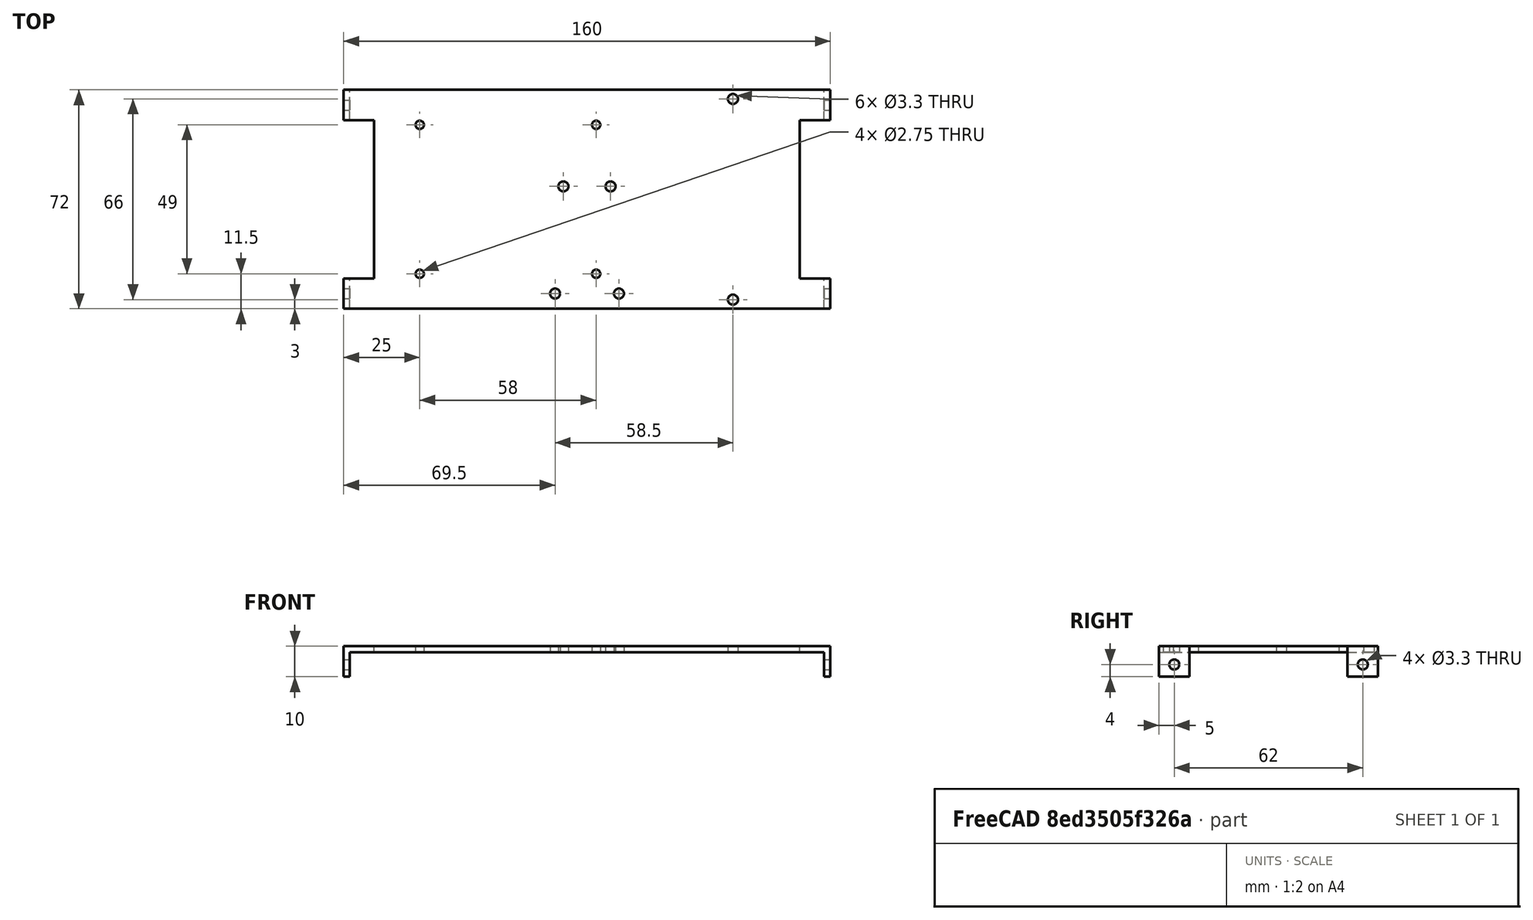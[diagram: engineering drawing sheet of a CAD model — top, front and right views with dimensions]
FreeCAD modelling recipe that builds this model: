
FCSTD DOCUMENT  (FreeCAD 0.17R13522 (Git))
Label: Zwischenblech_rpi
License: All rights reserved
LicenseURL: http://en.wikipedia.org/wiki/All_rights_reserved
objects: TechDraw::DrawViewDimension×25, Sketcher::SketchObject×4, PartDesign::Hole×4, Part::Box×3, Part::Cut×3, TechDraw::DrawProjGroupItem×3, Part::Mirroring×1, PartDesign::FeatureBase×1, TechDraw::DrawSVGTemplate×1, PartDesign::Body×1, TechDraw::DrawProjGroup×1, TechDraw::DrawPage×1
note: 21 computed .brp shape members not serialized (recipe doc carries the construction recipe); baked Part::Feature solids carry a one-line shape summary decoded from their .brp

FEATURE [Part::Box] Box  label="Würfel"
  AttacherType = Attacher::AttachEngine3D
  Height = 10
  Length = 160
  Width = 72
FEATURE [Part::Box] Box001  label="Würfel001"
  AttacherType = Attacher::AttachEngine3D
  Height = 10
  Length = 10
  Placement = pos=(0,10,0) rot=(0,0,1;0rad)
  Width = 52
FEATURE [Part::Mirroring] Part__Mirroring  label="Würfel001 (Mirror #1)"
  Base = (80,0,0)
  Normal = (1,0,0)
  Source = -> Box001
FEATURE [Part::Cut] Cut
  Base = -> Box
  Tool = -> Box001
FEATURE [Part::Cut] Cut001
  Base = -> Cut
  Tool = -> Part__Mirroring
FEATURE [Part::Box] Box002  label="Würfel002"
  AttacherType = Attacher::AttachEngine3D
  Height = 8
  Length = 156
  Placement = pos=(2,0,0) rot=(0,0,1;0rad)
  Width = 72
FEATURE [Part::Cut] Cut002
  Base = -> Cut001
  Tool = -> Box002
FEATURE [PartDesign::FeatureBase] BaseFeature
  BaseFeature = -> Cut002
FEATURE [Sketcher::SketchObject] Sketch
  MapMode = 5
  Placement = pos=(0,0,0) rot=(0.57735,-0.57735,-0.57735;2.0944rad)
  Support = -> [BaseFeature]
  sketch-geometry (2):
    g0: Circle CenterX=-5 CenterY=4 CenterZ=0 NormalX=0 NormalY=0 NormalZ=1 AngleXU=0 Radius=2.2
    g1: Circle CenterX=-67 CenterY=4 CenterZ=0 NormalX=0 NormalY=0 NormalZ=1 AngleXU=0 Radius=2.2
  constraints (6):
    c: Horizontal(g0,g1)
    c: DistanceY(g-1,g0) = 4
    c: Radius(g0) = 2.2
    c: Radius(g1) = 2.2
    c: DistanceX(g0,g-1) = 5
    c: DistanceX(g1,g-1) = 67
FEATURE [PartDesign::Hole] Hole
  BaseFeature = -> BaseFeature
  Depth = 25
  DepthType = 1
  Diameter = 3.3
  DrillPoint = 1
  DrillPointAngle = 118
  HoleCutCountersinkAngle = 90
  HoleCutDepth = 0
  HoleCutDiameter = 3
  HoleCutType = 0
  ModelActualThread = false
  Profile = -> Sketch
  Tapered = false
  TaperedAngle = 90
  ThreadAngle = 0
  ThreadClass = 0
  ThreadCutOffInner = 0
  ThreadCutOffOuter = 0
  ThreadDirection = 0
  ThreadFit = 0
  ThreadPitch = 0
  ThreadSize = 3
  ThreadType = 1
  Threaded = false
FEATURE [TechDraw::DrawSVGTemplate] Template
  EditableTexts = Designed_by_Name=Christian Dengler; FC-Date=25.04.2018; FC-SC=Scale; FC-SH=1/1; FC-Title=Zwischenblech, Oben
  Height = 210
  Orientation = 1
  Width = 297
FEATURE [Sketcher::SketchObject] Sketch001
  MapMode = 5
  Placement = pos=(0,0,10) rot=(0,0,1;0rad)
  Support = -> [Hole]
  sketch-geometry (4):
    g0: Circle CenterX=72.25 CenterY=40.25 CenterZ=0 NormalX=0 NormalY=0 NormalZ=1 AngleXU=0 Radius=1.65
    g1: Circle CenterX=87.75 CenterY=40.25 CenterZ=0 NormalX=0 NormalY=0 NormalZ=1 AngleXU=0 Radius=1.65
    g2: Circle CenterX=128 CenterY=69 CenterZ=0 NormalX=0 NormalY=0 NormalZ=1 AngleXU=0 Radius=2
    g3: Circle CenterX=128 CenterY=3 CenterZ=0 NormalX=0 NormalY=0 NormalZ=1 AngleXU=0 Radius=2
  constraints (12):
    c: Horizontal(g0,g1)
    c: Vertical(g2,g3)
    c: DistanceX(g-1,g0) = 72.25
    c: DistanceX(g0,g1) = 15.5
    c: DistanceY(g-1,g0) = 40.25
    c: Radius(g0) = 1.65
    c: Radius(g1) = 1.65
    c: DistanceY(g3,g2) = 66
    c: Radius(g2) = 2
    c: Radius(g3) = 2
    c: DistanceX(g-1,g3) = 128
    c: DistanceY(g-1,g3) = 3
FEATURE [Sketcher::SketchObject] Sketch002
  MapMode = 5
  Placement = pos=(0,0,10) rot=(0,0,1;0rad)
  Support = -> [Hole]
  sketch-geometry (4):
    g0: Circle CenterX=25 CenterY=60.5 CenterZ=0 NormalX=0 NormalY=0 NormalZ=1 AngleXU=0 Radius=1.375
    g1: Circle CenterX=83 CenterY=60.5 CenterZ=0 NormalX=0 NormalY=0 NormalZ=1 AngleXU=0 Radius=1.375
    g2: Circle CenterX=25 CenterY=11.5 CenterZ=0 NormalX=0 NormalY=0 NormalZ=1 AngleXU=0 Radius=1.375
    g3: Circle CenterX=83 CenterY=11.5 CenterZ=0 NormalX=0 NormalY=0 NormalZ=1 AngleXU=0 Radius=1.375
  constraints (12):
    c: Radius(g0) = 1.375
    c: Radius(g1) = 1.375
    c: Radius(g2) = 1.375
    c: Radius(g3) = 1.375
    c: Vertical(g2,g0)
    c: Vertical(g1,g3)
    c: Horizontal(g2,g3)
    c: Horizontal(g0,g1)
    c: DistanceY(g2,g0) = 49
    c: DistanceX(g2,g3) = 58
    c: DistanceX(g-1,g2) = 25
    c: DistanceY(g-1,g2) = 11.5
FEATURE [PartDesign::Hole] Hole001
  BaseFeature = -> Hole
  Depth = 25
  DepthType = 1
  Diameter = 3.3
  DrillPoint = 1
  DrillPointAngle = 118
  HoleCutCountersinkAngle = 90
  HoleCutDepth = 0
  HoleCutDiameter = 3
  HoleCutType = 0
  ModelActualThread = false
  Profile = -> Sketch001
  Tapered = false
  TaperedAngle = 90
  ThreadAngle = 0
  ThreadClass = 0
  ThreadCutOffInner = 0
  ThreadCutOffOuter = 0
  ThreadDirection = 0
  ThreadFit = 0
  ThreadPitch = 0
  ThreadSize = 3
  ThreadType = 1
  Threaded = false
FEATURE [PartDesign::Hole] Hole002
  BaseFeature = -> Hole001
  Depth = 25
  DepthType = 1
  Diameter = 2.75
  DrillPoint = 1
  DrillPointAngle = 118
  HoleCutCountersinkAngle = 90
  HoleCutDepth = 0
  HoleCutDiameter = 2.5
  HoleCutType = 0
  ModelActualThread = false
  Profile = -> Sketch002
  Tapered = false
  TaperedAngle = 90
  ThreadAngle = 0
  ThreadClass = 0
  ThreadCutOffInner = 0
  ThreadCutOffOuter = 0
  ThreadDirection = 0
  ThreadFit = 0
  ThreadPitch = 0
  ThreadSize = 2
  ThreadType = 1
  Threaded = false
FEATURE [Sketcher::SketchObject] Sketch003
  MapMode = 5
  Placement = pos=(0,0,10) rot=(0,0,1;0rad)
  Support = -> [Hole002]
  sketch-geometry (2):
    g0: Circle CenterX=69.5 CenterY=5 CenterZ=0 NormalX=0 NormalY=0 NormalZ=1 AngleXU=0 Radius=1.65
    g1: Circle CenterX=90.5 CenterY=5 CenterZ=0 NormalX=0 NormalY=0 NormalZ=1 AngleXU=0 Radius=1.65
  constraints (6):
    c: Horizontal(g0,g1)
    c: DistanceX(g0,g1) = 21
    c: Radius(g0) = 1.65
    c: Radius(g1) = 1.65
    c: DistanceX(g-1,g0) = 69.5
    c: DistanceY(g-1,g0) = 5
FEATURE [PartDesign::Hole] Hole003
  BaseFeature = -> Hole002
  Depth = 25
  DepthType = 0
  Diameter = 3.3
  DrillPoint = 1
  DrillPointAngle = 118
  HoleCutCountersinkAngle = 90
  HoleCutDepth = 0
  HoleCutDiameter = 3
  HoleCutType = 0
  ModelActualThread = false
  Profile = -> Sketch003
  Tapered = false
  TaperedAngle = 90
  ThreadAngle = 0
  ThreadClass = 0
  ThreadCutOffInner = 0
  ThreadCutOffOuter = 0
  ThreadDirection = 0
  ThreadFit = 0
  ThreadPitch = 0
  ThreadSize = 3
  ThreadType = 1
  Threaded = false
FEATURE [PartDesign::Body] Body
  BaseFeature = -> Cut002
  Group = -> [BaseFeature,Sketch,Hole,Sketch001,Sketch002,Hole001,Hole002,Sketch003,Hole003]
  Origin = -> Origin
  Tip = -> Hole003
FEATURE [TechDraw::DrawProjGroupItem] ProjItem001  label="Top"
  CoarseView = false
  Direction = (0,0,1)
  Focus = 100
  HardHidden = false
  IsoCount = 0
  IsoHidden = false
  IsoVisible = false
  LockPosition = false
  Perspective = false
  Rotation = 0
  RotationVector = (1,0,0)
  ScaleType = 0
  SeamHidden = false
  SeamVisible = false
  SmoothHidden = false
  SmoothVisible = false
  Source = -> [Body]
  Type = 4
  X = 0
  Y = -72.6
FEATURE [TechDraw::DrawProjGroupItem] ProjItem  label="Front"
  CoarseView = false
  Direction = (0,-1,0)
  Focus = 100
  HardHidden = false
  IsoCount = 0
  IsoHidden = false
  IsoVisible = false
  LockPosition = false
  Perspective = false
  Rotation = 0
  RotationVector = (1,0,0)
  ScaleType = 0
  SeamHidden = false
  SeamVisible = false
  SmoothHidden = false
  SmoothVisible = false
  Source = -> [Body]
  Type = 0
  X = 0
  Y = 63.9337
FEATURE [TechDraw::DrawProjGroupItem] ProjItem002  label="Left"
  CoarseView = false
  Direction = (-1,0,0)
  Focus = 100
  HardHidden = false
  IsoCount = 0
  IsoHidden = false
  IsoVisible = false
  LockPosition = true
  Perspective = false
  Rotation = 0
  RotationVector = (0,1,0)
  ScaleType = 0
  SeamHidden = false
  SeamVisible = false
  SmoothHidden = false
  SmoothVisible = false
  Source = -> [Body]
  Type = 1
  X = 132.721
  Y = 0
FEATURE [TechDraw::DrawProjGroup] ProjGroup
  Anchor = -> ProjItem
  AutoDistribute = true
  CubeDirs = (6) [(1.22465e-16,-2.44929e-16,-1),(1.93086e-32,-1,2.44929e-16),(-1,-2.46519e-32,-1.22465e-16),(-1.93086e-32,1,-2.44929e-16),(1,2.46519e-32,1.22465e-16),(-1.22465e-16,2.44929e-16,1)]
  CubeRotations = (6) [(1,2.46519e-32,1.22465e-16),(1,2.46519e-32,1.22465e-16),(4.89859e-16,1,-3.67394e-16),(-1,-2.46519e-32,-1.22465e-16),(-4.89859e-16,-1,3.67394e-16),(1,2.46519e-32,1.22465e-16)]
  LockPosition = false
  ProjectionType = 0
  Rotation = 0
  Scale = 0.8
  ScaleType = 2
  Source = -> [Body]
  Views = -> [ProjItem,ProjItem001,ProjItem002]
  X = 107.188
  Y = 189.377
  spacingX = 15
  spacingY = 15
FEATURE [TechDraw::DrawViewDimension] Dimension
  FormatSpec = %.2f
  LockPosition = false
  MeasureType = 1
  References2D = -> [ProjItem001]
  Rotation = 0
  ScaleType = 0
  Type = 1
  X = -5.19276
  Y = 38.5748
FEATURE [TechDraw::DrawViewDimension] Dimension001
  FormatSpec = %.2f
  LockPosition = false
  MeasureType = 1
  References2D = -> [ProjItem001]
  Rotation = 0
  ScaleType = 0
  Type = 1
  X = -6.12004
  Y = 46.7348
FEATURE [TechDraw::DrawViewDimension] Dimension002
  FormatSpec = %.2f
  LockPosition = false
  MeasureType = 1
  References2D = -> [ProjItem001]
  Rotation = 0
  ScaleType = 0
  Type = 1
  X = -6.86186
  Y = 55.8222
FEATURE [TechDraw::DrawViewDimension] Dimension003
  FormatSpec = %.2f
  LockPosition = false
  MeasureType = 1
  References2D = -> [ProjItem001]
  Rotation = 0
  ScaleType = 0
  Type = 2
  X = -90.1814
  Y = -6.72017
FEATURE [TechDraw::DrawViewDimension] Dimension004
  FormatSpec = %.2f
  LockPosition = false
  MeasureType = 1
  References2D = -> [ProjItem001]
  Rotation = 0
  ScaleType = 0
  Type = 1
  X = -25.9025
  Y = -54.5137
FEATURE [TechDraw::DrawViewDimension] Dimension006
  FormatSpec = %.2f
  LockPosition = false
  MeasureType = 1
  References2D = -> [ProjItem001]
  Rotation = 0
  ScaleType = 0
  Type = 1
  X = -24.0799
  Y = -97.174
FEATURE [TechDraw::DrawViewDimension] Dimension007
  FormatSpec = %.2f
  LockPosition = false
  MeasureType = 1
  References2D = -> [ProjItem001]
  Rotation = 0
  ScaleType = 0
  Type = 1
  X = -24.0703
  Y = -78.1047
FEATURE [TechDraw::DrawViewDimension] Dimension008
  FormatSpec = %.2f
  LockPosition = false
  MeasureType = 1
  References2D = -> [ProjItem001]
  Rotation = 0
  ScaleType = 0
  Type = 1
  X = -25.9902
  Y = -69.6317
FEATURE [TechDraw::DrawViewDimension] Dimension009
  FormatSpec = %.2f
  LockPosition = false
  MeasureType = 1
  References2D = -> [ProjItem001]
  Rotation = 0
  ScaleType = 0
  Type = 2
  X = -17.2304
  Y = -14.8229
FEATURE [TechDraw::DrawViewDimension] Dimension016
  FormatSpec = %.2f
  LockPosition = false
  MeasureType = 1
  References2D = -> [ProjItem001]
  Rotation = 0
  ScaleType = 0
  Type = 5
  X = 77.6975
  Y = 13.8504
FEATURE [TechDraw::DrawViewDimension] Dimension017
  FormatSpec = %.2f
  LockPosition = false
  MeasureType = 1
  References2D = -> [ProjItem001]
  Rotation = 0
  ScaleType = 0
  Type = 2
  X = 106.233
  Y = -3.81739
FEATURE [TechDraw::DrawViewDimension] Dimension018
  FormatSpec = %.2f
  LockPosition = false
  MeasureType = 1
  References2D = -> [ProjItem001]
  Rotation = 0
  ScaleType = 0
  Type = 2
  X = 132.397
  Y = -2.05268
FEATURE [TechDraw::DrawViewDimension] Dimension019
  FormatSpec = %.2f
  LockPosition = false
  MeasureType = 1
  References2D = -> [ProjItem001]
  Rotation = 0
  ScaleType = 0
  Type = 2
  X = 115.908
  Y = -3.4967
FEATURE [TechDraw::DrawViewDimension] Dimension020
  FormatSpec = %.2f
  LockPosition = false
  MeasureType = 1
  References2D = -> [ProjItem001]
  Rotation = 0
  ScaleType = 0
  Type = 5
  X = -32.4088
  Y = 8.84265
FEATURE [TechDraw::DrawViewDimension] Dimension021
  FormatSpec = %.2f
  LockPosition = false
  MeasureType = 1
  References2D = -> [ProjItem001]
  Rotation = 0
  ScaleType = 0
  Type = 5
  X = -30.8929
  Y = -3.40538
FEATURE [TechDraw::DrawViewDimension] Dimension022
  FormatSpec = %.2f
  LockPosition = false
  MeasureType = 1
  References2D = -> [ProjItem001]
  Rotation = 0
  ScaleType = 0
  Type = 5
  X = -31.75
  Y = 3.52366
FEATURE [TechDraw::DrawViewDimension] Dimension023
  FormatSpec = %.2f
  LockPosition = false
  MeasureType = 1
  References2D = -> [ProjItem001]
  Rotation = 0
  ScaleType = 0
  Type = 5
  X = -31.1566
  Y = -11.0161
FEATURE [TechDraw::DrawViewDimension] Dimension024
  FormatSpec = %.2f
  LockPosition = false
  MeasureType = 1
  References2D = -> [ProjItem001]
  Rotation = 0
  ScaleType = 0
  Type = 1
  X = -29.627
  Y = -33.5208
FEATURE [TechDraw::DrawViewDimension] Dimension025
  FormatSpec = %.2f
  LockPosition = false
  MeasureType = 1
  References2D = -> [ProjItem001]
  Rotation = 0
  ScaleType = 0
  Type = 2
  X = 24.7851
  Y = -8.32942
FEATURE [TechDraw::DrawViewDimension] Dimension026
  FormatSpec = %.2f
  LockPosition = false
  MeasureType = 1
  References2D = -> [ProjItem001]
  Rotation = 0
  ScaleType = 0
  Type = 5
  X = 26.2072
  Y = 13.4083
FEATURE [TechDraw::DrawViewDimension] Dimension027
  FormatSpec = %.2f
  LockPosition = false
  MeasureType = 1
  References2D = -> [ProjItem001]
  Rotation = 0
  ScaleType = 0
  Type = 5
  X = 45.7296
  Y = -49.4151
FEATURE [TechDraw::DrawViewDimension] Dimension028
  FormatSpec = %.2f
  LockPosition = false
  MeasureType = 1
  References2D = -> [ProjItem001]
  Rotation = 0
  ScaleType = 0
  Type = 2
  X = -72.9954
  Y = -9.34697
FEATURE [TechDraw::DrawViewDimension] Dimension029
  FormatSpec = %.2f
  LockPosition = false
  MeasureType = 1
  References2D = -> [ProjItem001]
  Rotation = 0
  ScaleType = 0
  Type = 2
  X = -81.007
  Y = -5.56367
FEATURE [TechDraw::DrawViewDimension] Dimension030
  FormatSpec = %.2f
  LockPosition = false
  MeasureType = 1
  References2D = -> [ProjItem001]
  Rotation = 0
  ScaleType = 0
  Type = 1
  X = -25.3703
  Y = -62.5357
FEATURE [TechDraw::DrawViewDimension] Dimension031
  FormatSpec = %.2f
  LockPosition = false
  MeasureType = 1
  References2D = -> [ProjItem001]
  Rotation = 0
  ScaleType = 0
  Type = 1
  X = -24.7027
  Y = -86.7933
FEATURE [TechDraw::DrawPage] Page
  KeepUpdated = true
  ProjectionType = 0
  Template = -> Template
  Views = -> [ProjGroup,Dimension,Dimension001,Dimension002,Dimension003,Dimension004,Dimension006,Dimension007,Dimension008,Dimension009,Dimension016,Dimension017,Dimension018,Dimension019,Dimension020,Dimension021,Dimension022,Dimension023,Dimension024,Dimension025,Dimension026,Dimension027,Dimension028,Dimension029,Dimension030,Dimension031]
